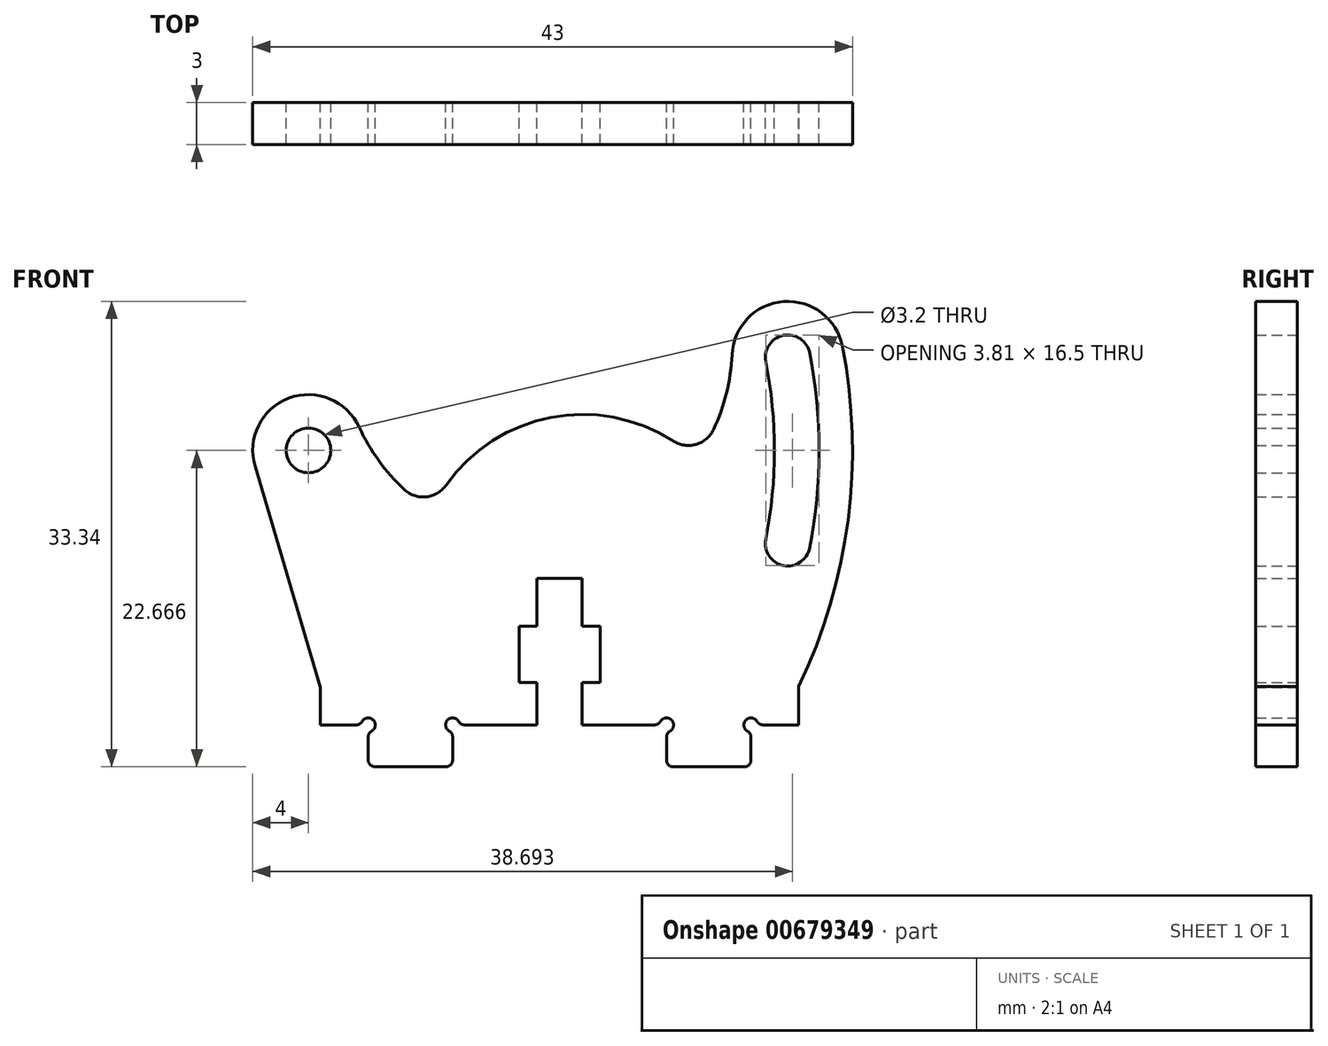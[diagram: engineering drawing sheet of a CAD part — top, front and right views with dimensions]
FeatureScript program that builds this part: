
annotation { "Feature Type Name" : "Feature", "Feature Type Description" : "" }
export const myFeature = defineFeature(function(context is Context, id is Id, definition is map)
    precondition{}
    {
        {
            var Q0;
            Q0=qCreatedBy(makeId("Front.planeOp"),FACE);
            var sketch = newSketch(context, id + "F0", { "sketchPlane" : qUnion([Q0])});
            skArc(sketch, "E0", {"start": v(-13.86, 7.66) * mm, "mid": v(-12.47, 5.26) * mm, "end": v(-10.63, 3.19) * mm});
            skArc(sketch, "E1", {"start": v(-13.86, 7.66) * mm, "mid": v(-18.9, 9.74) * mm, "end": v(-21.34, 4.86) * mm});
            skLineSegment(sketch, "E2", {"start": v(-21.34, 4.86) * mm, "end": v(-16.65, -11) * mm});
            skLineSegment(sketch, "E3", {"start": v(-16.65, -11) * mm, "end": v(-16.65, -13.67) * mm});
            skLineSegment(sketch, "E4", {"start": v(-16.65, -13.67) * mm, "end": v(-14.1, -13.67) * mm});
            skArc(sketch, "E5", {"start": v(-14.1, -13.67) * mm, "mid": v(-13.84, -13.6) * mm, "end": v(-13.66, -13.42) * mm});
            skArc(sketch, "E6", {"start": v(-12.97, -14.11) * mm, "mid": v(-12.86, -13.32) * mm, "end": v(-13.66, -13.42) * mm});
            skArc(sketch, "E7", {"start": v(-12.97, -14.11) * mm, "mid": v(-13.15, -14.3) * mm, "end": v(-13.22, -14.55) * mm});
            skLineSegment(sketch, "E8", {"start": v(-13.22, -14.55) * mm, "end": v(-13.22, -16.17) * mm});
            skArc(sketch, "E9", {"start": v(-13.22, -16.17) * mm, "mid": v(-13.07, -16.53) * mm, "end": v(-12.72, -16.67) * mm});
            skLineSegment(sketch, "E10", {"start": v(-12.72, -16.67) * mm, "end": v(-7.67, -16.67) * mm});
            skArc(sketch, "E11", {"start": v(-7.67, -16.67) * mm, "mid": v(-7.31, -16.53) * mm, "end": v(-7.17, -16.17) * mm});
            skLineSegment(sketch, "E12", {"start": v(-7.17, -16.17) * mm, "end": v(-7.17, -14.55) * mm});
            skArc(sketch, "E13", {"start": v(-7.17, -14.55) * mm, "mid": v(-7.23, -14.3) * mm, "end": v(-7.42, -14.11) * mm});
            skArc(sketch, "E14", {"start": v(-6.73, -13.42) * mm, "mid": v(-7.52, -13.32) * mm, "end": v(-7.42, -14.11) * mm});
            skArc(sketch, "E15", {"start": v(-6.73, -13.42) * mm, "mid": v(-6.54, -13.6) * mm, "end": v(-6.3, -13.67) * mm});
            skLineSegment(sketch, "E16", {"start": v(-6.3, -13.67) * mm, "end": v(-1.11, -13.67) * mm});
            skLineSegment(sketch, "E17", {"start": v(-1.11, -13.67) * mm, "end": v(-1.11, -10.65) * mm});
            skLineSegment(sketch, "E18", {"start": v(-1.11, -10.65) * mm, "end": v(-2.4, -10.65) * mm});
            skLineSegment(sketch, "E19", {"start": v(-2.4, -10.65) * mm, "end": v(-2.4, -6.61) * mm});
            skLineSegment(sketch, "E20", {"start": v(-2.4, -6.61) * mm, "end": v(-1.11, -6.61) * mm});
            skLineSegment(sketch, "E21", {"start": v(-1.11, -6.61) * mm, "end": v(-1.11, -3.17) * mm});
            skLineSegment(sketch, "E22", {"start": v(-1.11, -3.17) * mm, "end": v(2.11, -3.17) * mm});
            skLineSegment(sketch, "E23", {"start": v(2.11, -3.17) * mm, "end": v(2.11, -6.61) * mm});
            skLineSegment(sketch, "E24", {"start": v(2.11, -6.61) * mm, "end": v(3.4, -6.61) * mm});
            skLineSegment(sketch, "E25", {"start": v(3.4, -6.61) * mm, "end": v(3.4, -10.65) * mm});
            skLineSegment(sketch, "E26", {"start": v(3.4, -10.65) * mm, "end": v(2.11, -10.65) * mm});
            skLineSegment(sketch, "E27", {"start": v(2.11, -10.65) * mm, "end": v(2.11, -13.67) * mm});
            skLineSegment(sketch, "E28", {"start": v(2.11, -13.67) * mm, "end": v(7.3, -13.67) * mm});
            skArc(sketch, "E29", {"start": v(7.3, -13.67) * mm, "mid": v(7.54, -13.6) * mm, "end": v(7.73, -13.42) * mm});
            skArc(sketch, "E30", {"start": v(8.42, -14.11) * mm, "mid": v(8.52, -13.32) * mm, "end": v(7.73, -13.42) * mm});
            skArc(sketch, "E31", {"start": v(8.42, -14.11) * mm, "mid": v(8.23, -14.3) * mm, "end": v(8.17, -14.55) * mm});
            skLineSegment(sketch, "E32", {"start": v(8.17, -14.55) * mm, "end": v(8.17, -16.17) * mm});
            skArc(sketch, "E33", {"start": v(8.17, -16.17) * mm, "mid": v(8.31, -16.53) * mm, "end": v(8.67, -16.67) * mm});
            skLineSegment(sketch, "E34", {"start": v(8.67, -16.67) * mm, "end": v(13.72, -16.67) * mm});
            skArc(sketch, "E35", {"start": v(13.72, -16.67) * mm, "mid": v(14.07, -16.53) * mm, "end": v(14.22, -16.17) * mm});
            skLineSegment(sketch, "E36", {"start": v(14.22, -16.17) * mm, "end": v(14.22, -14.55) * mm});
            skArc(sketch, "E37", {"start": v(14.22, -14.55) * mm, "mid": v(14.15, -14.3) * mm, "end": v(13.97, -14.11) * mm});
            skArc(sketch, "E38", {"start": v(14.66, -13.42) * mm, "mid": v(13.86, -13.32) * mm, "end": v(13.97, -14.11) * mm});
            skArc(sketch, "E39", {"start": v(14.66, -13.42) * mm, "mid": v(14.84, -13.6) * mm, "end": v(15.1, -13.67) * mm});
            skLineSegment(sketch, "E40", {"start": v(15.1, -13.67) * mm, "end": v(17.65, -13.67) * mm});
            skLineSegment(sketch, "E41", {"start": v(17.65, -13.67) * mm, "end": v(17.65, -11) * mm});
            skArc(sketch, "E42", {"start": v(17.65, -11) * mm, "mid": v(17.65, -10.95) * mm, "end": v(17.65, -10.9) * mm});
            skLineSegment(sketch, "E43", {"start": v(17.65, -10.9) * mm, "end": v(17.65, -10.9) * mm});
            skArc(sketch, "E44", {"start": v(17.65, -10.9) * mm, "mid": v(21.18, 1.01) * mm, "end": v(20.78, 13.44) * mm});
            skArc(sketch, "E45", {"start": v(20.78, 13.44) * mm, "mid": v(16.56, 16.66) * mm, "end": v(12.86, 12.85) * mm});
            skArc(sketch, "E46", {"start": v(11.54, 7.5) * mm, "mid": v(12.46, 10.1) * mm, "end": v(12.86, 12.85) * mm});
            skArc(sketch, "E47", {"start": v(8.65, 6.67) * mm, "mid": v(10.28, 6.43) * mm, "end": v(11.54, 7.5) * mm});
            skArc(sketch, "E48", {"start": v(8.65, 6.67) * mm, "mid": v(-0.13, 8.35) * mm, "end": v(-7.64, 3.5) * mm});
            skArc(sketch, "E49", {"start": v(-10.63, 3.19) * mm, "mid": v(-9.06, 2.67) * mm, "end": v(-7.64, 3.5) * mm});
            skArc(sketch, "E50", {"start": v(18.43, -0.99) * mm, "mid": v(19.1, 6) * mm, "end": v(18.43, 12.98) * mm});
            skArc(sketch, "E51", {"start": v(15.29, -0.38) * mm, "mid": v(16.55, -2.25) * mm, "end": v(18.43, -0.99) * mm});
            skArc(sketch, "E52", {"start": v(15.29, -0.38) * mm, "mid": v(15.9, 6) * mm, "end": v(15.29, 12.37) * mm});
            skArc(sketch, "E53", {"start": v(18.43, 12.98) * mm, "mid": v(16.55, 14.24) * mm, "end": v(15.29, 12.37) * mm});
            skCircle(sketch, "E54", {"center": v(-17.5, 6) * mm, "radius": 1.6 * mm});
            skLineSegment(sketch, "E55", {"start": v(0.5, -3.17) * mm, "end": v(0.5, -17.13) * mm, "construction": true});
            skSolve(sketch);
        }
        {
            var Q0;
            Q0 = qSketchRegion(id + "F0", true);
            extrude(context, id + "F1", {"entities" : qUnion([Q0]), "depth" : 3 * mm, "offsetDistance" : 25 * mm});
        }
    });
